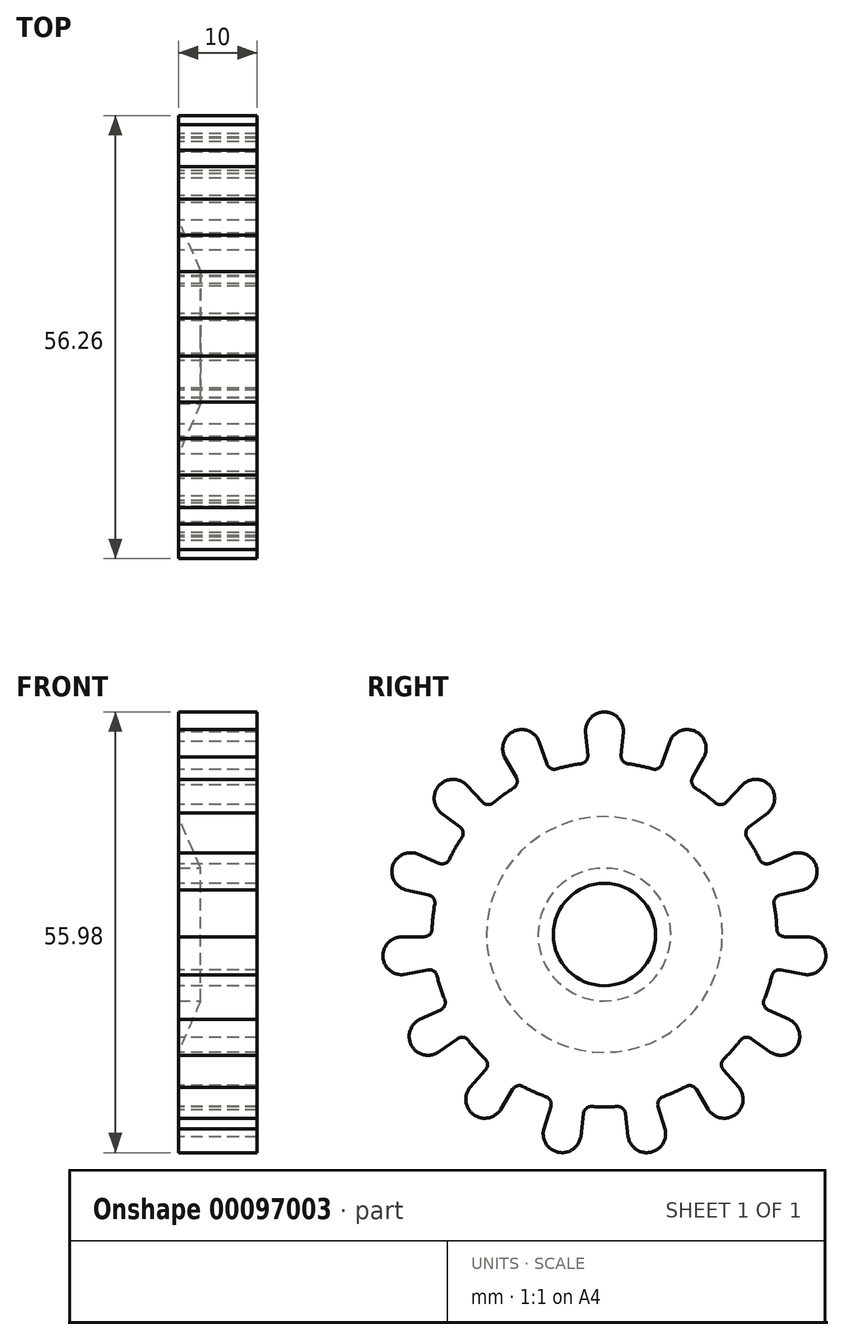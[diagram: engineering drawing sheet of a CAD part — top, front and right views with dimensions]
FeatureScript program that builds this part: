
annotation { "Feature Type Name" : "Feature", "Feature Type Description" : "" }
export const myFeature = defineFeature(function(context is Context, id is Id, definition is map)
    precondition{}
    {
        {
            var Q0;
            Q0=qCreatedBy(makeId("Right.planeOp"),FACE);
            var sketch = newSketch(context, id + "F0", { "sketchPlane" : qUnion([Q0])});
            skCircle(sketch, "E0", {"center": v(0, 0) * mm, "radius": 6.5 * mm});
            skCircle(sketch, "E1", {"center": v(0, 0) * mm, "radius": 21.9 * mm});
            skArc(sketch, "E2", {"start": v(2.38, 25.54) * mm, "mid": v(0, 28.28) * mm, "end": v(-2.38, 25.54) * mm});
            skLineSegment(sketch, "E3", {"start": v(-2.4, 25.76) * mm, "end": v(-2.03, 21.8) * mm});
            skLineSegment(sketch, "E4", {"start": v(2.4, 25.76) * mm, "end": v(2.03, 21.8) * mm});
            skSolve(sketch);
        }
        {
            var Q0;
            Q0=makeQuery(id+"F0.imprint","IMPRINT",FACE,{"disambiguationData":[TD([[makeQuery(id+"F0.imprint","IMPRINT",EDGE,{"derivedFrom":sQuery(id+"F0.wireOp",EDGE,"E0")}),-1.0]])]});
            var Q1;
            {var subQ0=sQuery(id+"F0.wireOp",EDGE,"E3");var subQ3=sQuery(id+"F0.wireOp",EDGE,"E1");var subQ4=makeQuery(id+"F0.imprint","INTERSECT",VERTEX,{"derivedFrom":[subQ3,subQ0]});Q1=makeQuery(id+"F0.imprint","IMPRINT",FACE,{"disambiguationData":[TD([[makeQuery(id+"F0.imprint","IMPRINT",EDGE,{"disambiguationData":[TD([[subQ4,1.0]])],"derivedFrom":subQ3}),-1.0]])]});}
            extrude(context, id + "F1", {"entities" : qUnion([Q0, Q1]), "endBound" : BoundingType.SYMMETRIC, "depth" : 10 * mm});
        }
        {
            var Q0;
            Q0=makeQuery(id+"F1.opExtrude","SWEPT_EDGE",EDGE,{"disambiguationData":[OSD([sQuery(id+"F0.wireOp",EDGE,"E1"),sQuery(id+"F0.wireOp",EDGE,"E3")])]});
            fillet(context, id + "F2", {"entities" : qUnion([Q0]), "radius" : 1 * mm, "tangentPropagation" : true, "allowEdgeOverflow" : false});
        }
        {
            var Q0;
            Q0=makeQuery(id+"F1.opExtrude","SWEPT_EDGE",EDGE,{"disambiguationData":[OSD([sQuery(id+"F0.wireOp",EDGE,"E1"),sQuery(id+"F0.wireOp",EDGE,"E4")])]});
            fillet(context, id + "F3", {"entities" : qUnion([Q0]), "radius" : 1 * mm, "tangentPropagation" : true, "allowEdgeOverflow" : false});
        }
        {
            var Q0;
            Q0=makeQuery(id+"F1.opExtrude","SWEPT_FACE",FACE,{"disambiguationData":[OSD([sQuery(id+"F0.wireOp",EDGE,"E3")])]});
            var Q1;
            Q1=makeQuery(id+"F1.opExtrude","SWEPT_FACE",FACE,{"disambiguationData":[OSD([sQuery(id+"F0.wireOp",EDGE,"E2")])]});
            var Q2;
            Q2=makeQuery(id+"F2.opFillet","BLEND_FACE",FACE,{"disambiguationData":[OSD([sQuery(id+"F0.wireOp",EDGE,"E1"),sQuery(id+"F0.wireOp",EDGE,"E3")])]});
            var Q3;
            Q3=makeQuery(id+"F1.opExtrude","SWEPT_FACE",FACE,{"disambiguationData":[OSD([sQuery(id+"F0.wireOp",EDGE,"E4")])]});
            var Q4;
            Q4=makeQuery(id+"F3.opFillet","BLEND_FACE",FACE,{"disambiguationData":[OSD([sQuery(id+"F0.wireOp",EDGE,"E1"),sQuery(id+"F0.wireOp",EDGE,"E4")])]});
            var Q5;
            Q5=makeQuery(id+"F1.opExtrude","CAP_EDGE",EDGE,{"disambiguationData":[OSD([sQuery(id+"F0.wireOp",EDGE,"E0")])],"isStart":false});
            circularPattern(context, id + "F5", {"patternType" : PatternType.FACE, "faces" : qUnion([Q0, Q1, Q2, Q3, Q4]), "axis" : qUnion([Q5]), "angle" : 24 * degree, "instanceCount" : 15});
        }
        {
            var Q0;
            Q0=qCreatedBy(makeId("Front.planeOp"),FACE);
            var sketch = newSketch(context, id + "F6", { "sketchPlane" : qUnion([Q0])});
            skLineSegment(sketch, "E5", {"start": v(0, 0) * mm, "end": v(0, 8.43) * mm});
            skLineSegment(sketch, "E6", {"start": v(0, 8.43) * mm, "end": v(0, 8.43) * mm});
            skLineSegment(sketch, "E7", {"start": v(-2.18, 8.43) * mm, "end": v(-5.07, 15.15) * mm});
            skLineSegment(sketch, "E8", {"start": v(-5.07, 15.15) * mm, "end": v(-5.14, 8.43) * mm});
            skLineSegment(sketch, "E9", {"start": v(-5.14, 8.43) * mm, "end": v(-2.18, 8.43) * mm});
            skSolve(sketch);
        }
        {
            var Q0;
            Q0 = qSketchRegion(id + "F6", true);
            var Q1;
            Q1=makeQuery(id+"F1.opExtrude","SWEPT_FACE",FACE,{"disambiguationData":[OSD([sQuery(id+"F0.wireOp",EDGE,"E0")])]});
            revolve(context, id + "F7", {"operationType" : NewBodyOperationType.REMOVE, "entities" : qUnion([Q0]), "axis" : qUnion([Q1]), "revolveType" : RevolveType.FULL, "oppositeDirection" : true});
        }
    });
